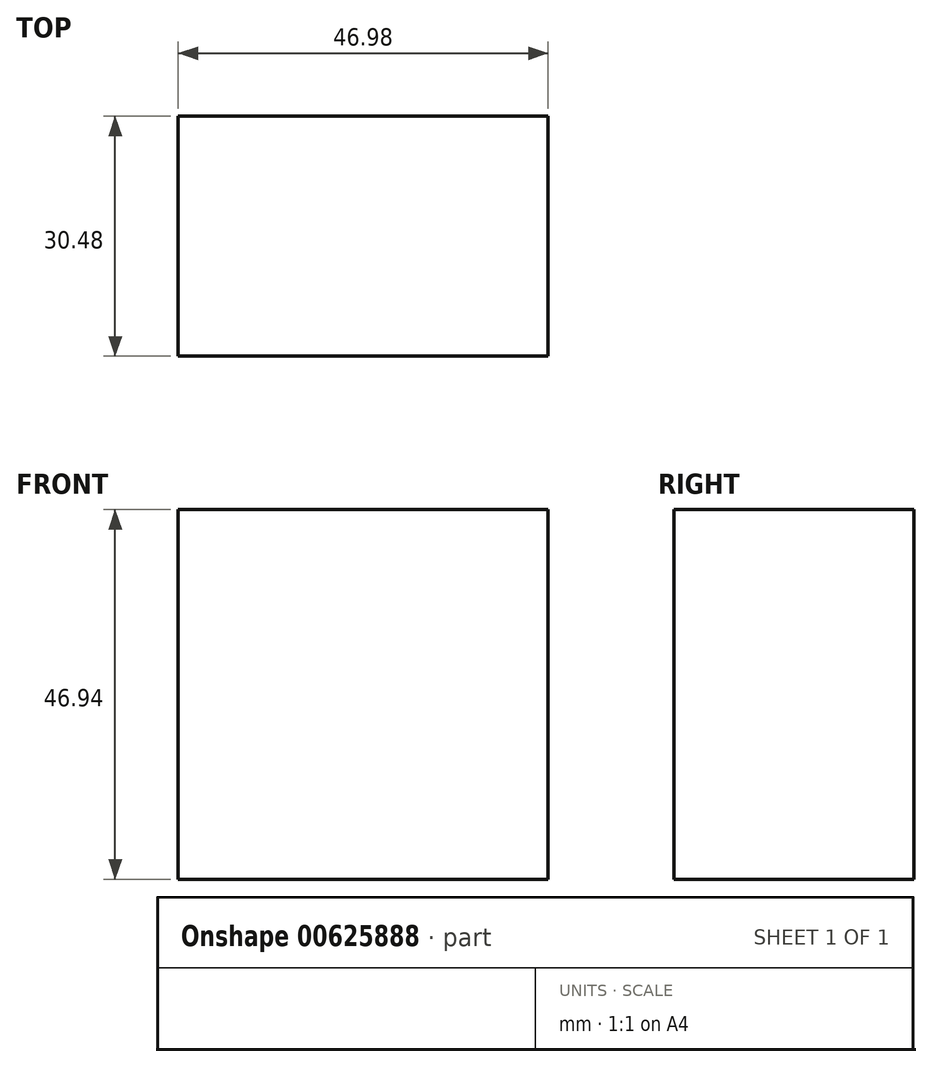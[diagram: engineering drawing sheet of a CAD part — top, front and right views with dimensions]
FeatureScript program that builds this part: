
annotation { "Feature Type Name" : "Feature", "Feature Type Description" : "" }
export const myFeature = defineFeature(function(context is Context, id is Id, definition is map)
    precondition{}
    {
        {
            var Q0;
            Q0=qCreatedBy(makeId("Front.planeOp"),FACE);
            var sketch = newSketch(context, id + "F0", { "sketchPlane" : qUnion([Q0])});
            skLineSegment(sketch, "E0", {"start": v(-85.9, 17.25) * mm, "end": v(-53.91, 48.24) * mm});
            skSolve(sketch);
        }
        {
            var Q0;
            Q0=sQuery(id+"F0.wireOp",EDGE,"E0");
            extrude(context, id + "F1", {"bodyType" : ToolBodyType.SURFACE, "surfaceEntities" : qUnion([Q0]), "depth" : 30.48 * mm, "offsetDistance" : 30.48 * mm});
        }
        {
            var Q0;
            Q0=qCreatedBy(makeId("Front.planeOp"),FACE);
            var sketch = newSketch(context, id + "F2", { "sketchPlane" : qUnion([Q0])});
            skLineSegment(sketch, "E1.bottom", {"start": v(-118.92, -20.5) * mm, "end": v(-71.94, -20.5) * mm});
            skLineSegment(sketch, "E1.top", {"start": v(-118.92, -67.45) * mm, "end": v(-71.94, -67.45) * mm});
            skLineSegment(sketch, "E1.left", {"start": v(-118.92, -20.5) * mm, "end": v(-118.92, -67.45) * mm});
            skLineSegment(sketch, "E1.right", {"start": v(-71.94, -20.5) * mm, "end": v(-71.94, -67.45) * mm});
            skSolve(sketch);
        }
        {
            var Q0;
            Q0 = qSketchRegion(id + "F2", true);
            extrude(context, id + "F3", {"entities" : qUnion([Q0]), "depth" : 30.48 * mm, "offsetDistance" : 30.48 * mm});
        }
    });
